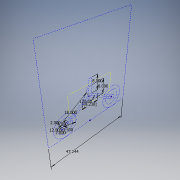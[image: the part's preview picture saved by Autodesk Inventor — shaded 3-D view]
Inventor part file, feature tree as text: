
AUTODESK INVENTOR PART (.ipt)
format: ipt  version: 2019 (Build 230136000, 136)  size: 111,104 bytes
history: native  units: in
note: dims shown in document units (in); Inventor stores cm internally (conversion verified against a paired STEP export)
features: sketch x1
ambient origin geometry x8: Origin, YZ Plane, XZ Plane, XY Plane, X Axis, Y Axis, Z Axis, Center Point
feature tree (1):
  sketch  "Sketch1"  dims[d0=47.2441in d1=12.0in d2=2.0in d3=18.0in d4=4.0in d5=2.0in d6=120.0deg d7=8.0in d10=8.0in d11=9.2376in d12=3.5in]
